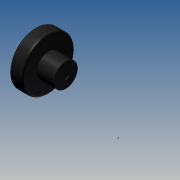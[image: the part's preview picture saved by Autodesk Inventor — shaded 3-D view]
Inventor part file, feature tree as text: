
AUTODESK INVENTOR PART (.ipt)
format: ipt  version: 2011 (Build 150239000, 239)  size: 115,200 bytes
history: native  units: mm
features: sketch x4, extrude x2, revolve x1, fillet x1
ambient origin geometry x8: Origin, YZ Plane, XZ Plane, XY Plane, X Axis, Y Axis, Z Axis, Center Point
bodies: Solid1 (feature_tree)
feature tree (8):
  sketch  "Sketch1"  dims[d87=12.03mm d90=3.175mm d92=90.0deg]
  revolve  "Revolution1"  [1 undecoded]
  sketch  "Sketch10"  dims[d100=0.1mm d101=0.0mm]
  fillet  "Fillet11"  [1 undecoded]
  extrude  "Extrusion7"  Depth=2.1mm TaperAngle=0.0deg
  extrude  "Extrusion10"  [1 undecoded]
  sketch  "Sketch9"  dims[d93=0.2mm d94=2.1mm d95=0.0mm]
  sketch  "Sketch12"
note: 3 required parameter values undecoded (feature->parameter linkage not recoverable at this tier; creation-order binding heuristic only, values carry confidence <= 0.55)